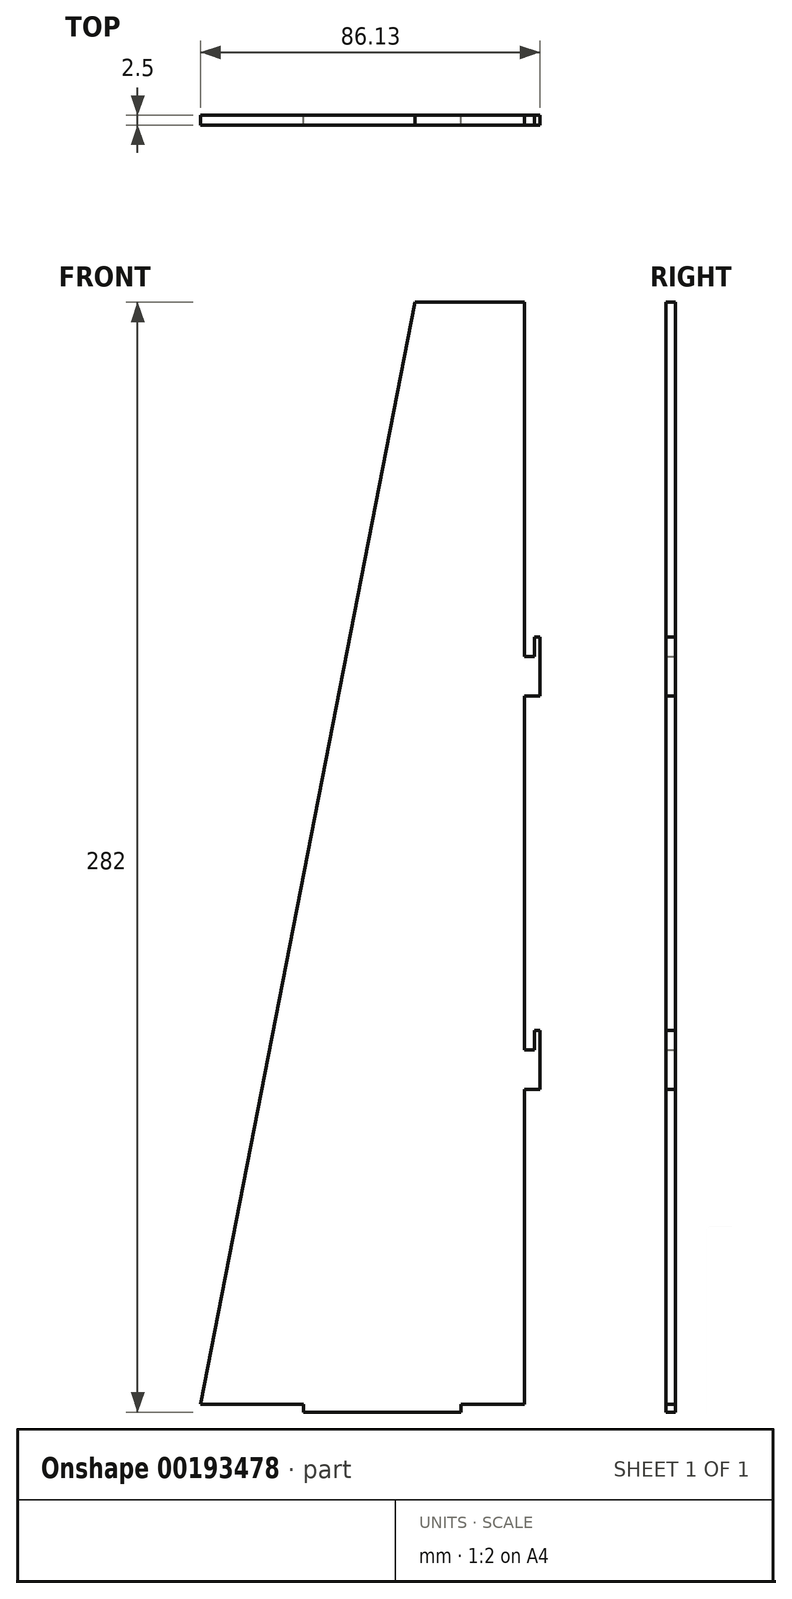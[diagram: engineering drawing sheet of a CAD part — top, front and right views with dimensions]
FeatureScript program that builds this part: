
annotation { "Feature Type Name" : "Feature", "Feature Type Description" : "" }
export const myFeature = defineFeature(function(context is Context, id is Id, definition is map)
    precondition{}
    {
        {
            var Q0;
            Q0=qCreatedBy(makeId("Front.planeOp"),FACE);
            var sketch = newSketch(context, id + "F0", { "sketchPlane" : qUnion([Q0])});
            skLineSegment(sketch, "E0", {"start": v(-86.13, 0) * mm, "end": v(-31.7, 280) * mm});
            skLineSegment(sketch, "E1", {"start": v(-31.7, 280) * mm, "end": v(0, 280) * mm});
            skLineSegment(sketch, "E2", {"start": v(0, 280) * mm, "end": v(0, 0) * mm});
            skLineSegment(sketch, "E3", {"start": v(0, 0) * mm, "end": v(-20, 0) * mm});
            skLineSegment(sketch, "E4", {"start": v(-60, 0) * mm, "end": v(-60, -2) * mm});
            skLineSegment(sketch, "E5", {"start": v(-60, -2) * mm, "end": v(-20, -2) * mm});
            skLineSegment(sketch, "E6", {"start": v(-20, -2) * mm, "end": v(-20, 0) * mm});
            skLineSegment(sketch, "E7.trimOffspring", {"start": v(-60, 0) * mm, "end": v(-86.13, 0) * mm});
            skSolve(sketch);
        }
        {
            var Q0;
            Q0=qSketchRegion(id+"F0",true);
            extrude(context, id + "F1", {"entities" : qUnion([Q0]), "depth" : 2.5 * mm});
        }
        {
            var Q0;
            Q0=qCreatedBy(makeId("Front.planeOp"),FACE);
            var sketch = newSketch(context, id + "F2", { "sketchPlane" : qUnion([Q0])});
            skLineSegment(sketch, "E8", {"start": v(26.57, 285.47) * mm, "end": v(-3.83, 285.47) * mm});
            skLineSegment(sketch, "E9", {"start": v(-3.83, 285.47) * mm, "end": v(-3.83, 190) * mm});
            skLineSegment(sketch, "E10", {"start": v(-3.83, 180) * mm, "end": v(-3.83, 90) * mm});
            skLineSegment(sketch, "E11.0.1.5", {"start": v(-3.83, 80) * mm, "end": v(-3.83, -10) * mm});
            skLineSegment(sketch, "E11.direction2", {"start": v(-1.33, 175) * mm, "end": v(-1.33, 75) * mm, "construction": true});
            skLineSegment(sketch, "E12", {"start": v(-3.83, -10) * mm, "end": v(26.57, -10) * mm});
            skLineSegment(sketch, "E13", {"start": v(26.57, -10) * mm, "end": v(26.57, 285.47) * mm});
            skLineSegment(sketch, "E14", {"start": v(-3.83, 190) * mm, "end": v(-1.33, 190) * mm});
            skLineSegment(sketch, "E15", {"start": v(-1.33, 190) * mm, "end": v(-1.33, 195) * mm});
            skLineSegment(sketch, "E16", {"start": v(-1.33, 195) * mm, "end": v(3.67, 195) * mm});
            skLineSegment(sketch, "E17", {"start": v(3.67, 195) * mm, "end": v(3.67, 180) * mm});
            skLineSegment(sketch, "E18", {"start": v(3.67, 180) * mm, "end": v(-3.83, 180) * mm});
            skLineSegment(sketch, "E19.0.1.0", {"start": v(-1.33, 90) * mm, "end": v(-1.33, 95) * mm});
            skLineSegment(sketch, "E19.0.1.1", {"start": v(-1.33, 95) * mm, "end": v(3.67, 95) * mm});
            skLineSegment(sketch, "E19.0.1.2", {"start": v(3.67, 95) * mm, "end": v(3.67, 80) * mm});
            skLineSegment(sketch, "E19.0.1.3", {"start": v(3.67, 80) * mm, "end": v(-3.83, 80) * mm});
            skLineSegment(sketch, "E19.0.1.4", {"start": v(-3.83, 90) * mm, "end": v(-1.33, 90) * mm});
            skLineSegment(sketch, "E19.direction1", {"start": v(-3.83, 180) * mm, "end": v(21.17, 180) * mm, "construction": true});
            skLineSegment(sketch, "E19.direction2", {"start": v(-3.83, 180) * mm, "end": v(-3.83, 80) * mm, "construction": true});
            skSolve(sketch);
        }
        {
            var Q0;
            Q0=qSketchRegion(id+"F2",true);
            extrude(context, id + "F3", {"entities" : qUnion([Q0]), "operationType" : NewBodyOperationType.REMOVE, "depth" : 25 * mm});
        }
    });
